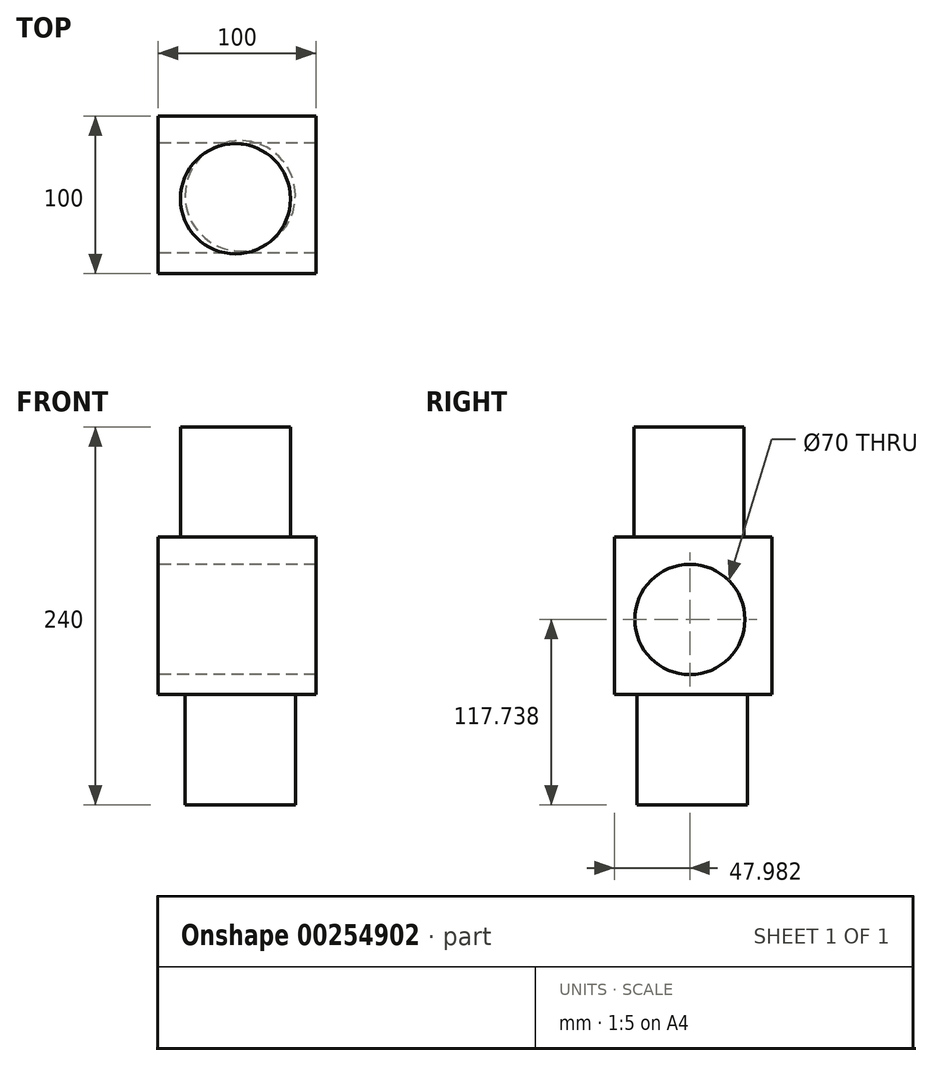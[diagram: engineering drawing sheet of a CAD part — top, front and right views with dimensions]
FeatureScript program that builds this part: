
annotation { "Feature Type Name" : "Feature", "Feature Type Description" : "" }
export const myFeature = defineFeature(function(context is Context, id is Id, definition is map)
    precondition{}
    {
        {
            var Q0;
            Q0=qCreatedBy(makeId("Front.planeOp"),FACE);
            var sketch = newSketch(context, id + "F0", { "sketchPlane" : qUnion([Q0])});
            skLineSegment(sketch, "E0.bottom", {"start": v(0, 0) * mm, "end": v(100, 0) * mm});
            skLineSegment(sketch, "E0.top", {"start": v(0, 100) * mm, "end": v(100, 100) * mm});
            skLineSegment(sketch, "E0.left", {"start": v(0, 0) * mm, "end": v(0, 100) * mm});
            skLineSegment(sketch, "E0.right", {"start": v(100, 0) * mm, "end": v(100, 100) * mm});
            skSolve(sketch);
        }
        {
            var Q0;
            Q0=makeQuery(id+"F0.imprint","IMPRINT",FACE,{"disambiguationData":[TD([[makeQuery(id+"F0.imprint","IMPRINT",EDGE,{"derivedFrom":sQuery(id+"F0.wireOp",EDGE,"E0.bottom")}),1.0]])]});
            extrude(context, id + "F1", {"entities" : qUnion([Q0]), "depth" : 100 * mm});
        }
        {
            var Q0;
            Q0=makeQuery(id+"F1.opExtrude","SWEPT_FACE",FACE,{"disambiguationData":[OSD([sQuery(id+"F0.wireOp",EDGE,"E0.top")])]});
            var sketch = newSketch(context, id + "F2", { "sketchPlane" : qUnion([Q0])});
            skCircle(sketch, "E1", {"center": v(48.98, -52.55) * mm, "radius": 35 * mm});
            skSolve(sketch);
        }
        {
            var Q0;
            Q0=makeQuery(id+"F2.imprint","IMPRINT",FACE,{"disambiguationData":[TD([[makeQuery(id+"F2.imprint","IMPRINT",EDGE,{"derivedFrom":sQuery(id+"F2.wireOp",EDGE,"E1")}),1.0]])]});
            extrude(context, id + "F3", {"entities" : qUnion([Q0]), "operationType" : NewBodyOperationType.ADD, "depth" : 70 * mm});
        }
        {
            var Q0;
            Q0=makeQuery(id+"F1.opExtrude","SWEPT_FACE",FACE,{"disambiguationData":[OSD([sQuery(id+"F0.wireOp",EDGE,"E0.bottom")])]});
            var sketch = newSketch(context, id + "F4", { "sketchPlane" : qUnion([Q0])});
            skCircle(sketch, "E2", {"center": v(52.02, 50.59) * mm, "radius": 35 * mm});
            skSolve(sketch);
        }
        {
            var Q0;
            Q0=makeQuery(id+"F4.imprint","IMPRINT",FACE,{"disambiguationData":[TD([[makeQuery(id+"F4.imprint","IMPRINT",EDGE,{"derivedFrom":sQuery(id+"F4.wireOp",EDGE,"E2")}),1.0]])]});
            extrude(context, id + "F5", {"entities" : qUnion([Q0]), "operationType" : NewBodyOperationType.ADD, "depth" : 70 * mm});
        }
        {
            var Q0;
            Q0=makeQuery(id+"F1.opExtrude","SWEPT_FACE",FACE,{"disambiguationData":[OSD([sQuery(id+"F0.wireOp",EDGE,"E0.left")])]});
            var sketch = newSketch(context, id + "F6", { "sketchPlane" : qUnion([Q0])});
            skCircle(sketch, "E3", {"center": v(52.02, 47.74) * mm, "radius": 35 * mm});
            skSolve(sketch);
        }
        {
            var Q0;
            Q0=makeQuery(id+"F6.imprint","IMPRINT",FACE,{"disambiguationData":[TD([[makeQuery(id+"F6.imprint","IMPRINT",EDGE,{"derivedFrom":sQuery(id+"F6.wireOp",EDGE,"E3")}),1.0]])]});
            extrude(context, id + "F7", {"entities" : qUnion([Q0]), "operationType" : NewBodyOperationType.REMOVE, "oppositeDirection" : true, "depth" : 100 * mm});
        }
    });
